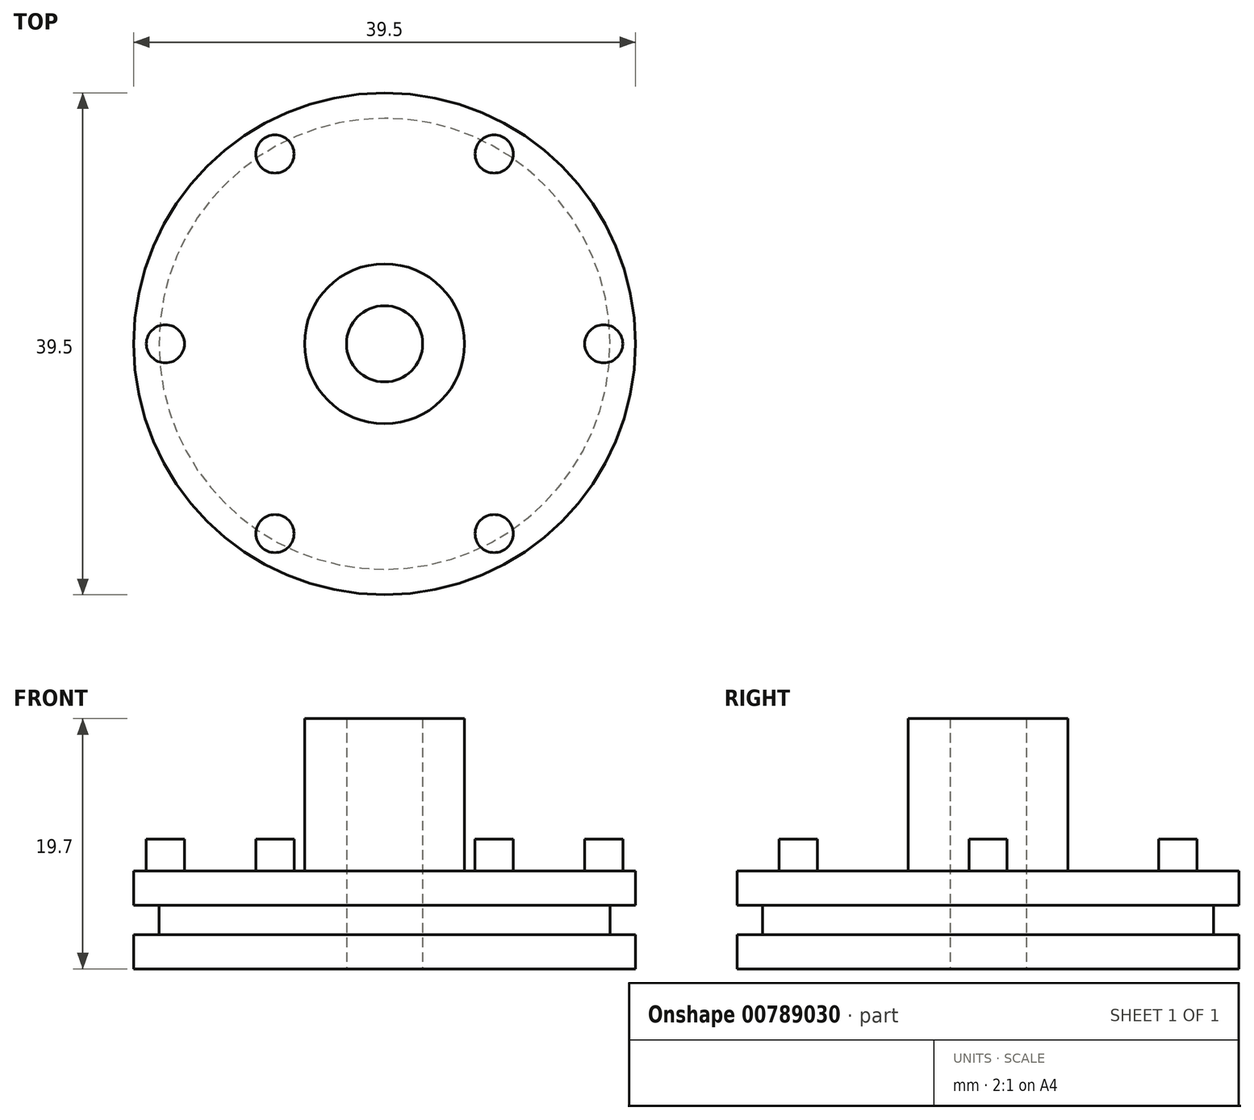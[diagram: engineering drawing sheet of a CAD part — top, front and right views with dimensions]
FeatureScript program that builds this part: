
annotation { "Feature Type Name" : "Feature", "Feature Type Description" : "" }
export const myFeature = defineFeature(function(context is Context, id is Id, definition is map)
    precondition{}
    {
        {
            var Q0;
            Q0=qCreatedBy(makeId("Front.planeOp"),FACE);
            var sketch = newSketch(context, id + "F0", { "sketchPlane" : qUnion([Q0])});
            skLineSegment(sketch, "E0", {"start": v(-19.75, 0) * mm, "end": v(0, 0) * mm});
            skLineSegment(sketch, "E1", {"start": v(0, 0) * mm, "end": v(0, 19.7) * mm});
            skLineSegment(sketch, "E2", {"start": v(0, 19.7) * mm, "end": v(-6.3, 19.7) * mm});
            skLineSegment(sketch, "E3", {"start": v(-6.3, 19.7) * mm, "end": v(-6.3, 7.7) * mm});
            skLineSegment(sketch, "E4", {"start": v(-6.3, 7.7) * mm, "end": v(-19.75, 7.7) * mm});
            skLineSegment(sketch, "E5", {"start": v(-3, 19.7) * mm, "end": v(-3, 0) * mm});
            skLineSegment(sketch, "E6", {"start": v(-19.75, 7.7) * mm, "end": v(-19.75, 5) * mm});
            skLineSegment(sketch, "E7", {"start": v(-19.75, 0) * mm, "end": v(-19.75, 2.7) * mm});
            skLineSegment(sketch, "E8", {"start": v(-19.75, 5) * mm, "end": v(-17.75, 5) * mm});
            skLineSegment(sketch, "E9", {"start": v(-17.75, 5) * mm, "end": v(-17.75, 2.7) * mm});
            skLineSegment(sketch, "E10", {"start": v(-17.75, 2.7) * mm, "end": v(-19.75, 2.7) * mm});
            skSolve(sketch);
        }
        {
            var Q0;
            {var subQ0=sQuery(id+"F0.wireOp",EDGE,"E3");Q0=makeQuery(id+"F0.imprint","IMPRINT",FACE,{"disambiguationData":[TD([[makeQuery(id+"F0.imprint","IMPRINT",EDGE,{"derivedFrom":subQ0}),1.0]])]});}
            var Q1;
            Q1=sQuery(id+"F0.wireOp",EDGE,"E1");
            revolve(context, id + "F1", {"surfaceOperationType" : NewSurfaceOperationType.NEW, "entities" : qUnion([Q0]), "axis" : qUnion([Q1]), "revolveType" : RevolveType.FULL});
        }
        {
            var Q0;
            Q0=makeQuery(id+"F1.opRevolve","SWEPT_FACE",FACE,{"disambiguationData":[OSD([sQuery(id+"F0.wireOp",EDGE,"E4")])]});
            var sketch = newSketch(context, id + "F2", { "sketchPlane" : qUnion([Q0])});
            skCircle(sketch, "E11.cCircle", {"center": v(0, 0) * mm, "radius": 14.94 * mm, "construction": true});
            skLineSegment(sketch, "E11.0", {"start": v(-8.62, -14.94) * mm, "end": v(8.62, -14.94) * mm, "construction": true});
            skLineSegment(sketch, "E11.1", {"start": v(-17.25, 0) * mm, "end": v(-8.62, -14.94) * mm, "construction": true});
            skLineSegment(sketch, "E11.2", {"start": v(-8.62, 14.94) * mm, "end": v(-17.25, 0) * mm, "construction": true});
            skLineSegment(sketch, "E11.3", {"start": v(8.62, 14.94) * mm, "end": v(-8.62, 14.94) * mm, "construction": true});
            skLineSegment(sketch, "E11.4", {"start": v(17.25, 0) * mm, "end": v(8.62, 14.94) * mm, "construction": true});
            skLineSegment(sketch, "E11.5", {"start": v(8.62, -14.94) * mm, "end": v(17.25, 0) * mm, "construction": true});
            skPoint(sketch, "E11.0.midPoint", {"position": v(0, -14.94) * mm});
            skCircle(sketch, "E12", {"center": v(-8.62, 14.94) * mm, "radius": 1.5 * mm});
            skCircle(sketch, "E13", {"center": v(8.62, 14.94) * mm, "radius": 1.5 * mm});
            skCircle(sketch, "E14", {"center": v(17.25, 0) * mm, "radius": 1.5 * mm});
            skCircle(sketch, "E15", {"center": v(8.62, -14.94) * mm, "radius": 1.5 * mm});
            skCircle(sketch, "E16", {"center": v(-8.62, -14.94) * mm, "radius": 1.5 * mm});
            skCircle(sketch, "E17", {"center": v(-17.25, 0) * mm, "radius": 1.5 * mm});
            skSolve(sketch);
        }
        {
            var Q0;
            Q0 = qSketchRegion(id + "F2", true);
            extrude(context, id + "F3", {"entities" : qUnion([Q0]), "operationType" : NewBodyOperationType.ADD, "depth" : 2.5 * mm, "offsetDistance" : 25 * mm});
        }
    });
